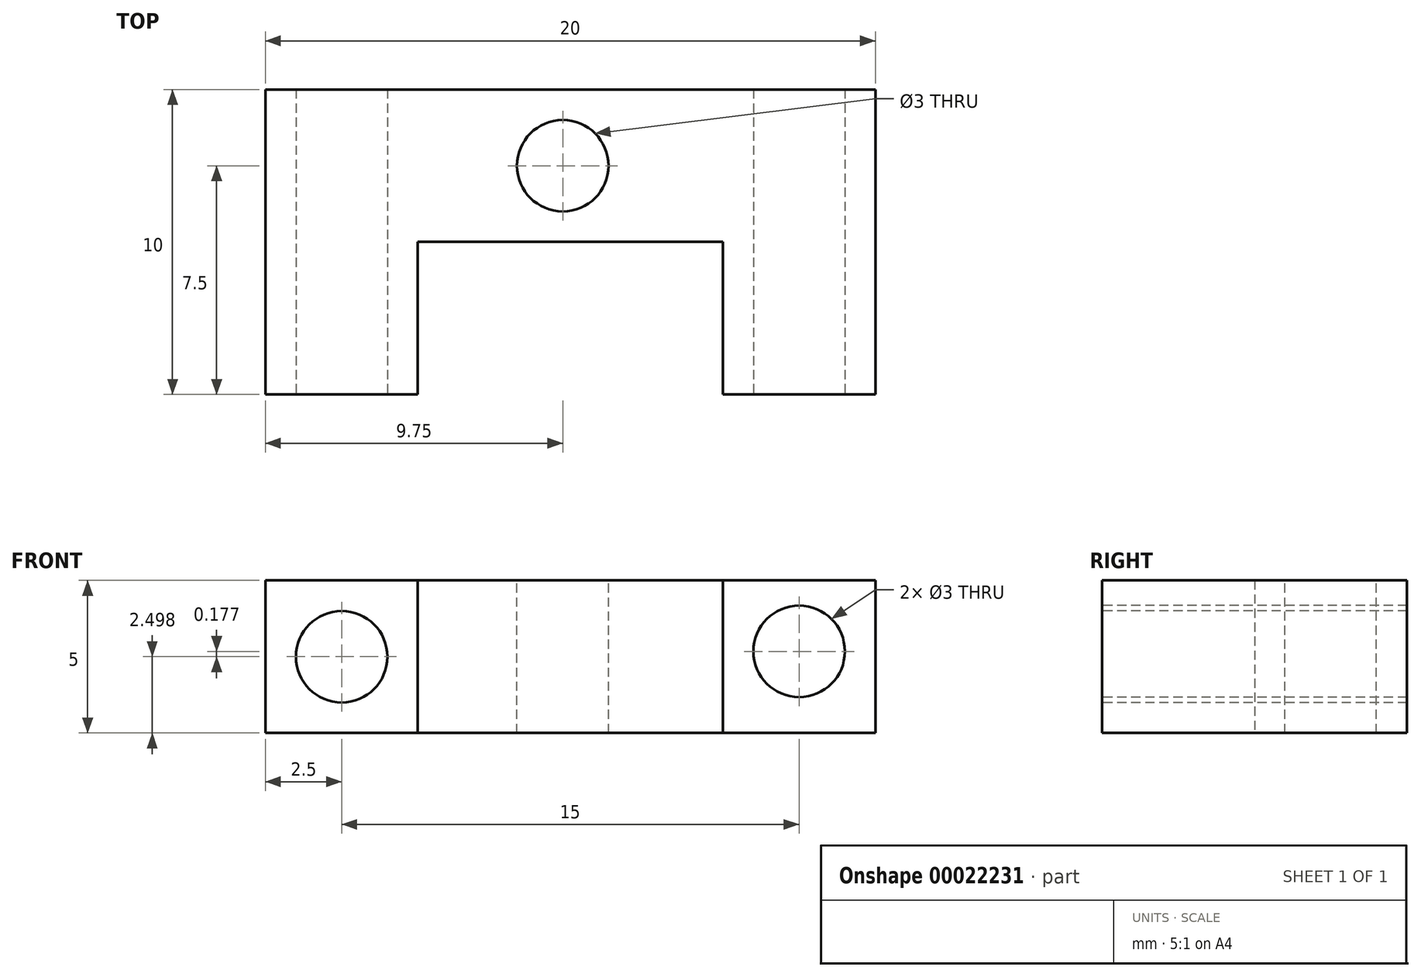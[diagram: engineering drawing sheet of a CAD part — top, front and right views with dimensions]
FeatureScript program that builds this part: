
annotation { "Feature Type Name" : "Feature", "Feature Type Description" : "" }
export const myFeature = defineFeature(function(context is Context, id is Id, definition is map)
    precondition{}
    {
        {
            var Q0;
            Q0=qCreatedBy(makeId("Top.planeOp"),FACE);
            var sketch = newSketch(context, id + "F0", { "sketchPlane" : qUnion([Q0])});
            skLineSegment(sketch, "E0", {"start": v(0, 0) * mm, "end": v(-5, 0) * mm});
            skLineSegment(sketch, "E1", {"start": v(-5, 0) * mm, "end": v(-5, 10) * mm});
            skLineSegment(sketch, "E2", {"start": v(-5, 10) * mm, "end": v(15, 10) * mm});
            skLineSegment(sketch, "E3", {"start": v(15, 10) * mm, "end": v(15, 0) * mm});
            skLineSegment(sketch, "E4", {"start": v(15, 0) * mm, "end": v(10, 0) * mm});
            skLineSegment(sketch, "E5", {"start": v(10, 0) * mm, "end": v(10, 5) * mm});
            skLineSegment(sketch, "E6", {"start": v(10, 5) * mm, "end": v(0, 5) * mm});
            skLineSegment(sketch, "E7", {"start": v(0, 5) * mm, "end": v(0, 0) * mm});
            skSolve(sketch);
        }
        {
            var Q0;
            Q0=makeQuery(id+"F0.imprint","IMPRINT",FACE,{"disambiguationData":[TD([[makeQuery(id+"F0.imprint","IMPRINT",EDGE,{"derivedFrom":sQuery(id+"F0.wireOp",EDGE,"E0")}),-1.0]])]});
            extrude(context, id + "F1", {"entities" : qUnion([Q0]), "depth" : 5 * mm});
        }
        {
            var Q0;
            Q0=makeQuery(id+"F1.opExtrude","SWEPT_FACE",FACE,{"disambiguationData":[OSD([sQuery(id+"F0.wireOp",EDGE,"E0")])]});
            var sketch = newSketch(context, id + "F2", { "sketchPlane" : qUnion([Q0])});
            skCircle(sketch, "E8", {"center": v(-2.5, 2.5) * mm, "radius": 1.5 * mm});
            skCircle(sketch, "E9", {"center": v(12.5, 2.67) * mm, "radius": 1.5 * mm});
            skSolve(sketch);
        }
        {
            var Q0;
            Q0=makeQuery(id+"F2.imprint","IMPRINT",FACE,{"disambiguationData":[TD([[makeQuery(id+"F2.imprint","IMPRINT",EDGE,{"derivedFrom":sQuery(id+"F2.wireOp",EDGE,"E9")}),1.0]])]});
            var Q1;
            Q1=makeQuery(id+"F2.imprint","IMPRINT",FACE,{"disambiguationData":[TD([[makeQuery(id+"F2.imprint","IMPRINT",EDGE,{"derivedFrom":sQuery(id+"F2.wireOp",EDGE,"E8")}),1.0]])]});
            extrude(context, id + "F3", {"entities" : qUnion([Q0, Q1]), "operationType" : NewBodyOperationType.REMOVE, "oppositeDirection" : true, "depth" : 25 * mm});
        }
        {
            var Q0;
            Q0=makeQuery(id+"F1.opExtrude","CAP_FACE",FACE,{"disambiguationData":[OSD([sQuery(id+"F0.wireOp",EDGE,"E0"),sQuery(id+"F0.wireOp",EDGE,"E1"),sQuery(id+"F0.wireOp",EDGE,"E2"),sQuery(id+"F0.wireOp",EDGE,"E3"),sQuery(id+"F0.wireOp",EDGE,"E4"),sQuery(id+"F0.wireOp",EDGE,"E5"),sQuery(id+"F0.wireOp",EDGE,"E6"),sQuery(id+"F0.wireOp",EDGE,"E7")])],"isStart":false});
            var sketch = newSketch(context, id + "F4", { "sketchPlane" : qUnion([Q0])});
            skCircle(sketch, "E10", {"center": v(4.75, 7.5) * mm, "radius": 1.5 * mm});
            skSolve(sketch);
        }
        {
            var Q0;
            Q0=makeQuery(id+"F4.imprint","IMPRINT",FACE,{"disambiguationData":[TD([[makeQuery(id+"F4.imprint","IMPRINT",EDGE,{"derivedFrom":sQuery(id+"F4.wireOp",EDGE,"E10")}),1.0]])]});
            extrude(context, id + "F5", {"entities" : qUnion([Q0]), "operationType" : NewBodyOperationType.REMOVE, "oppositeDirection" : true, "depth" : 25 * mm});
        }
    });
